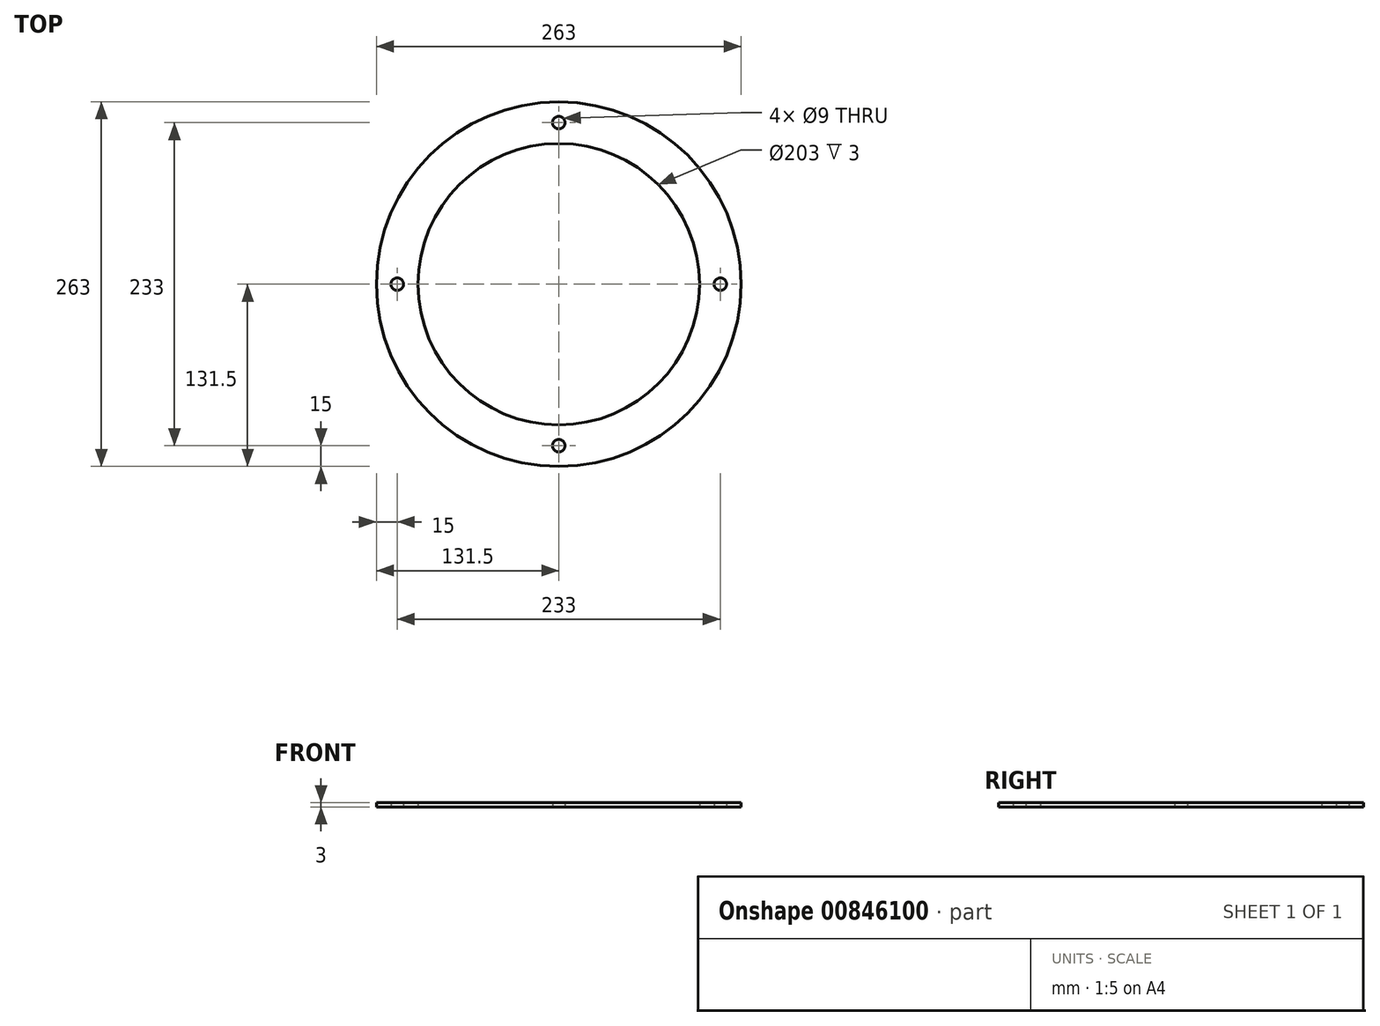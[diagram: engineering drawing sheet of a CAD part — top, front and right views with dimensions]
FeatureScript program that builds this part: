
annotation { "Feature Type Name" : "Feature", "Feature Type Description" : "" }
export const myFeature = defineFeature(function(context is Context, id is Id, definition is map)
    precondition{}
    {
        {
            var Q0;
            Q0=qCreatedBy(makeId("Top.planeOp"),FACE);
            var sketch = newSketch(context, id + "F0", { "sketchPlane" : qUnion([Q0])});
            skCircle(sketch, "E0", {"center": v(0, 0) * mm, "radius": 101.5 * mm});
            skCircle(sketch, "E1", {"center": v(0, 0) * mm, "radius": 131.5 * mm});
            skCircle(sketch, "E2", {"center": v(0, 116.5) * mm, "radius": 4.5 * mm});
            skCircle(sketch, "E3.1.0", {"center": v(116.5, 0) * mm, "radius": 4.5 * mm});
            skCircle(sketch, "E3.2.0", {"center": v(0, -116.5) * mm, "radius": 4.5 * mm});
            skCircle(sketch, "E3.3.0", {"center": v(-116.5, 0) * mm, "radius": 4.5 * mm});
            skLineSegment(sketch, "E3.anchor1", {"start": v(0, 0) * mm, "end": v(0, 116.5) * mm, "construction": true});
            skLineSegment(sketch, "E3.anchor2", {"start": v(0, 0) * mm, "end": v(-116.5, 0) * mm, "construction": true});
            skSolve(sketch);
        }
        {
            var Q0;
            Q0=makeQuery(id+"F0.imprint","IMPRINT",FACE,{"disambiguationData":[TD([[makeQuery(id+"F0.imprint","IMPRINT",EDGE,{"derivedFrom":sQuery(id+"F0.wireOp",EDGE,"E0")}),-1.0]])]});
            extrude(context, id + "F1", {"entities" : qUnion([Q0]), "depth" : 3 * mm, "offsetDistance" : 25 * mm});
        }
    });
